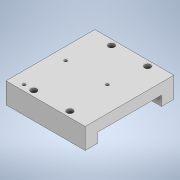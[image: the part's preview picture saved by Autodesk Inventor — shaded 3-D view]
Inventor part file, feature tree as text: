
AUTODESK INVENTOR PART (.ipt)
format: ipt  version: 2020 (Build 240168000, 168)  size: 136,704 bytes
history: native  units: mm
features: sketch x3, extrude x2, hole x2
ambient origin geometry x8: Origin, YZ Plane, XZ Plane, XY Plane, X Axis, Y Axis, Z Axis, Center Point
bodies: Solid1 (feature_tree)
feature tree (7):
  extrude  "Extrusion1"  Depth=64.0mm
  sketch  "Sketch2"  dims[d2=8.0mm d3=0.0mm d4=26.0mm]
  extrude  "Extrusion2"  Depth=8.0mm
  hole  "Hole1"  [1 undecoded]
  hole  "Hole2"  [1 undecoded]
  sketch  "Sketch1"  dims[d0=57.0mm d1=64.0mm]
  sketch  "Sketch3"  dims[d5=16.0mm d6=4.0mm d7=4.0mm d8=4.0mm d9=4.0mm d10=26.0mm d11=16.0mm d12=9.0mm d13=9.0mm d14=7.0mm d15=0.0mm d16=4.3mm d17=6.0mm d18=4.0mm d19=2.0mm d20=90.0deg d21=8.0mm d22=20.594885mm d28=4.0mm d30=9.0mm d33=2.05mm d34=6.0mm d35=4.0mm d36=2.0mm d37=90.0deg d38=8.0mm d39=20.594885mm d41=30.0mm d42=30.0mm]
note: 2 required parameter values undecoded (feature->parameter linkage not recoverable at this tier; creation-order binding heuristic only, values carry confidence <= 0.55)
